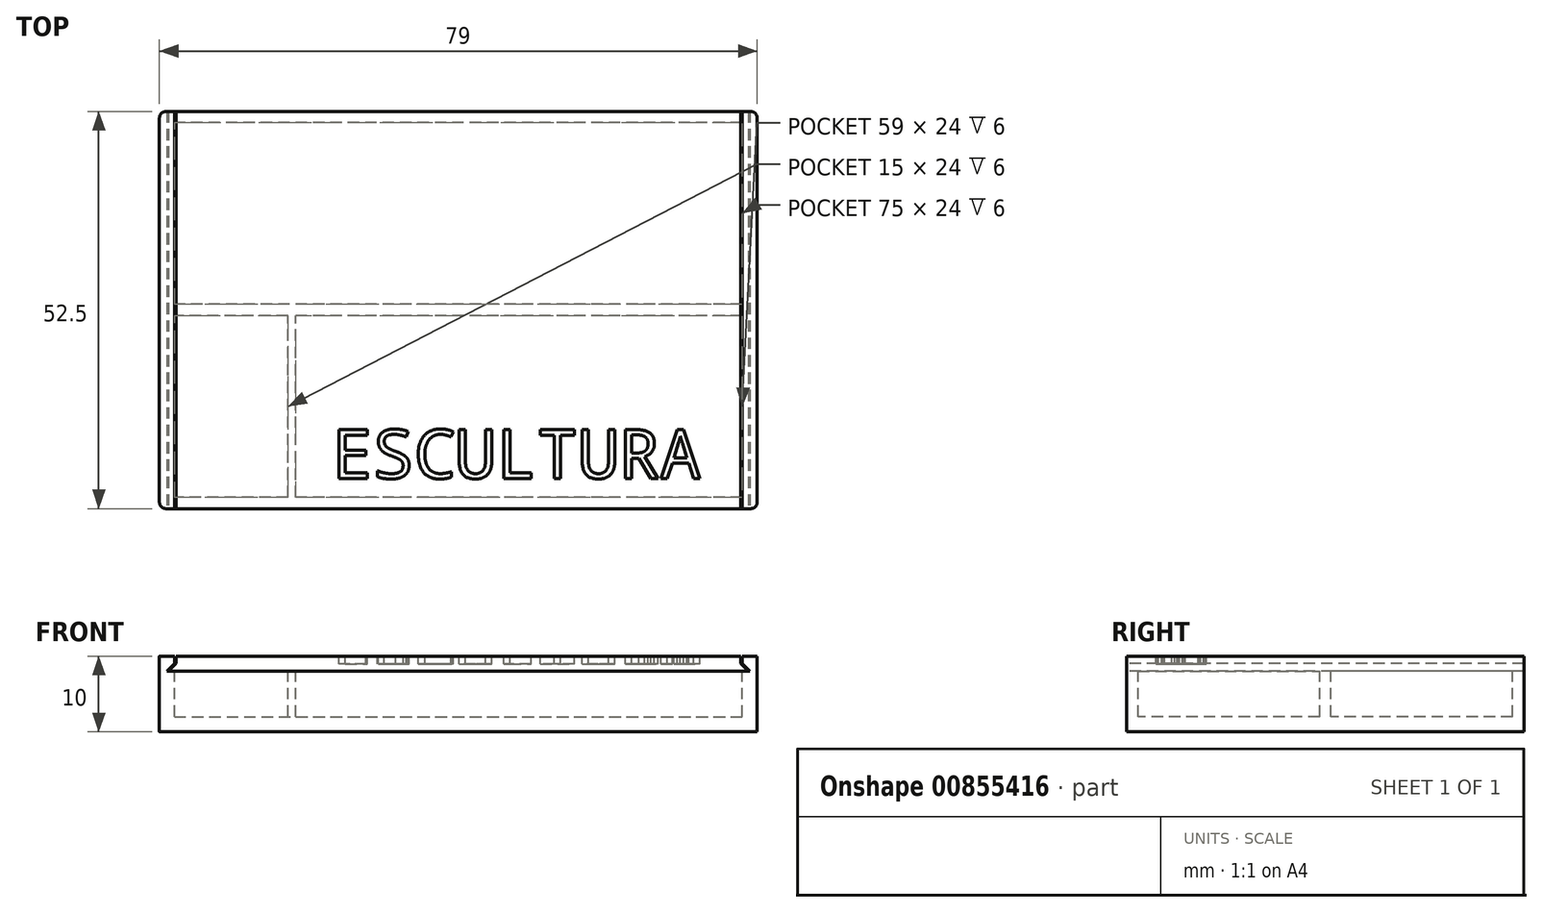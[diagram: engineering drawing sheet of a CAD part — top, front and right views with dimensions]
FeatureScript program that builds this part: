
annotation { "Feature Type Name" : "Feature", "Feature Type Description" : "" }
export const myFeature = defineFeature(function(context is Context, id is Id, definition is map)
    precondition{}
    {
        {
            var Q0;
            Q0=qCreatedBy(makeId("Top.planeOp"),FACE);
            var sketch = newSketch(context, id + "F0", { "sketchPlane" : qUnion([Q0])});
            skLineSegment(sketch, "E0.bottom", {"start": v(-39.5, 26.25) * mm, "end": v(39.5, 26.25) * mm});
            skLineSegment(sketch, "E0.top", {"start": v(-39.5, -26.25) * mm, "end": v(39.5, -26.25) * mm});
            skLineSegment(sketch, "E0.left", {"start": v(-39.5, 26.25) * mm, "end": v(-39.5, -26.25) * mm});
            skLineSegment(sketch, "E0.right", {"start": v(39.5, 26.25) * mm, "end": v(39.5, -26.25) * mm});
            skLineSegment(sketch, "E1", {"start": v(0, 0) * mm, "end": v(0, 26.25) * mm, "construction": true});
            skLineSegment(sketch, "E2", {"start": v(0, 0) * mm, "end": v(39.5, 0) * mm, "construction": true});
            skLineSegment(sketch, "E3.bottom", {"start": v(-37.5, 24.75) * mm, "end": v(37.5, 24.75) * mm});
            skLineSegment(sketch, "E3.top", {"start": v(-37.5, 0.75) * mm, "end": v(37.5, 0.75) * mm});
            skLineSegment(sketch, "E3.left", {"start": v(-37.5, 24.75) * mm, "end": v(-37.5, 0.75) * mm});
            skLineSegment(sketch, "E3.right", {"start": v(37.5, 24.75) * mm, "end": v(37.5, 0.75) * mm});
            skLineSegment(sketch, "E4.bottom", {"start": v(-37.5, -0.75) * mm, "end": v(-22.5, -0.75) * mm});
            skLineSegment(sketch, "E4.top", {"start": v(-37.5, -24.75) * mm, "end": v(-22.5, -24.75) * mm});
            skLineSegment(sketch, "E4.left", {"start": v(-37.5, -0.75) * mm, "end": v(-37.5, -24.75) * mm});
            skLineSegment(sketch, "E4.right", {"start": v(-22.5, -0.75) * mm, "end": v(-22.5, -24.75) * mm});
            skLineSegment(sketch, "E5.bottom", {"start": v(-21.5, -0.75) * mm, "end": v(37.5, -0.75) * mm});
            skLineSegment(sketch, "E5.top", {"start": v(-21.5, -24.75) * mm, "end": v(37.5, -24.75) * mm});
            skLineSegment(sketch, "E5.left", {"start": v(-21.5, -0.75) * mm, "end": v(-21.5, -24.75) * mm});
            skLineSegment(sketch, "E5.right", {"start": v(37.5, -0.75) * mm, "end": v(37.5, -24.75) * mm});
            skSolve(sketch);
        }
        {
            var Q0;
            Q0=makeQuery(id+"F0.imprint","IMPRINT",FACE,{"disambiguationData":[TD([[makeQuery(id+"F0.imprint","IMPRINT",EDGE,{"derivedFrom":sQuery(id+"F0.wireOp",EDGE,"E5.bottom")}),-1.0]])]});
            var Q1;
            Q1=makeQuery(id+"F0.imprint","IMPRINT",FACE,{"disambiguationData":[TD([[makeQuery(id+"F0.imprint","IMPRINT",EDGE,{"derivedFrom":sQuery(id+"F0.wireOp",EDGE,"E0.bottom")}),-1.0]])]});
            var Q2;
            Q2=makeQuery(id+"F0.imprint","IMPRINT",FACE,{"disambiguationData":[TD([[makeQuery(id+"F0.imprint","IMPRINT",EDGE,{"derivedFrom":sQuery(id+"F0.wireOp",EDGE,"E3.bottom")}),-1.0]])]});
            var Q3;
            Q3=makeQuery(id+"F0.imprint","IMPRINT",FACE,{"disambiguationData":[TD([[makeQuery(id+"F0.imprint","IMPRINT",EDGE,{"derivedFrom":sQuery(id+"F0.wireOp",EDGE,"E4.bottom")}),-1.0]])]});
            extrude(context, id + "F1", {"entities" : qUnion([Q0, Q1, Q2, Q3]), "oppositeDirection" : true, "depth" : 10 * mm, "offsetDistance" : 25 * mm});
        }
        {
            var Q0;
            Q0=makeQuery(id+"F0.imprint","IMPRINT",FACE,{"disambiguationData":[TD([[makeQuery(id+"F0.imprint","IMPRINT",EDGE,{"derivedFrom":sQuery(id+"F0.wireOp",EDGE,"E3.bottom")}),-1.0]])]});
            var Q1;
            Q1=makeQuery(id+"F0.imprint","IMPRINT",FACE,{"disambiguationData":[TD([[makeQuery(id+"F0.imprint","IMPRINT",EDGE,{"derivedFrom":sQuery(id+"F0.wireOp",EDGE,"E4.bottom")}),-1.0]])]});
            var Q2;
            Q2=makeQuery(id+"F0.imprint","IMPRINT",FACE,{"disambiguationData":[TD([[makeQuery(id+"F0.imprint","IMPRINT",EDGE,{"derivedFrom":sQuery(id+"F0.wireOp",EDGE,"E5.bottom")}),-1.0]])]});
            extrude(context, id + "F2", {"entities" : qUnion([Q0, Q1, Q2]), "operationType" : NewBodyOperationType.REMOVE, "oppositeDirection" : true, "depth" : 8 * mm, "offsetDistance" : 25 * mm});
        }
        {
            var Q0;
            Q0=makeQuery(id+"F0.imprint","IMPRINT",FACE,{"disambiguationData":[TD([[makeQuery(id+"F0.imprint","IMPRINT",EDGE,{"derivedFrom":sQuery(id+"F0.wireOp",EDGE,"E0.bottom")}),-1.0]])]});
            var sketch = newSketch(context, id + "F3", { "sketchPlane" : qUnion([Q0])});
            skLineSegment(sketch, "E6.0", {"start": v(-37.5, 25.25) * mm, "end": v(-37.5, 0.75) * mm});
            skLineSegment(sketch, "E6.1", {"start": v(37.5, 24.75) * mm, "end": v(37.5, 0.75) * mm});
            skLineSegment(sketch, "E7.0", {"start": v(-37.5, -0.75) * mm, "end": v(-37.5, -25.25) * mm});
            skLineSegment(sketch, "E7.1", {"start": v(37.5, -0.75) * mm, "end": v(37.5, -25.25) * mm});
            skLineSegment(sketch, "E8.bottom", {"start": v(-37.5, 27.25) * mm, "end": v(37.5, 27.25) * mm});
            skLineSegment(sketch, "E8.top", {"start": v(-37.5, -27.25) * mm, "end": v(37.5, -27.25) * mm});
            skLineSegment(sketch, "E8.left", {"start": v(-37.5, 27.25) * mm, "end": v(-37.5, -27.25) * mm});
            skLineSegment(sketch, "E8.right", {"start": v(37.5, 27.25) * mm, "end": v(37.5, -27.25) * mm});
            skSolve(sketch);
        }
        {
            var Q0;
            Q0 = qSketchRegion(id + "F3", true);
            extrude(context, id + "F4", {"entities" : qUnion([Q0]), "operationType" : NewBodyOperationType.REMOVE, "oppositeDirection" : true, "depth" : 2 * mm, "offsetDistance" : 25 * mm});
        }
        {
            var Q0;
            Q0=makeQuery(id+"F1.opExtrude","SWEPT_FACE",FACE,{"disambiguationData":[OSD([sQuery(id+"F0.wireOp",EDGE,"E0.top")])]});
            var sketch = newSketch(context, id + "F5", { "sketchPlane" : qUnion([Q0])});
            skLineSegment(sketch, "E9", {"start": v(-37.5, -2) * mm, "end": v(-38.5, -2) * mm});
            skLineSegment(sketch, "E10", {"start": v(-38.5, -2) * mm, "end": v(-37.5, -1) * mm});
            skLineSegment(sketch, "E11", {"start": v(-37.5, -1) * mm, "end": v(-37.5, -2) * mm});
            skLineSegment(sketch, "E12", {"start": v(0, 0) * mm, "end": v(0, -10) * mm, "construction": true});
            skLineSegment(sketch, "E13.MirrorCS", {"start": v(38.5, -2) * mm, "end": v(37.5, -1) * mm});
            skLineSegment(sketch, "E14.MirrorCS", {"start": v(37.5, -1) * mm, "end": v(37.5, -2) * mm});
            skLineSegment(sketch, "E15.MirrorCS", {"start": v(37.5, -2) * mm, "end": v(38.5, -2) * mm});
            skSolve(sketch);
        }
        {
            var Q0;
            Q0 = qSketchRegion(id + "F5", true);
            extrude(context, id + "F6", {"entities" : qUnion([Q0]), "operationType" : NewBodyOperationType.REMOVE, "endBound" : BoundingType.THROUGH_ALL, "oppositeDirection" : true, "depth" : 25 * mm, "offsetDistance" : 25 * mm});
        }
        {
            var Q0;
            Q0=makeQuery(id+"F1.opExtrude","SWEPT_FACE",FACE,{"disambiguationData":[OSD([sQuery(id+"F0.wireOp",EDGE,"E0.top")])]});
            var sketch = newSketch(context, id + "F7", { "sketchPlane" : qUnion([Q0])});
            skLineSegment(sketch, "E16", {"start": v(-37.3, 0) * mm, "end": v(-37.3, -1) * mm});
            skLineSegment(sketch, "E17", {"start": v(-37.3, -1) * mm, "end": v(-38.3, -2) * mm});
            skLineSegment(sketch, "E18", {"start": v(-38.3, -2) * mm, "end": v(38.3, -2) * mm});
            skLineSegment(sketch, "E19", {"start": v(38.3, -2) * mm, "end": v(37.3, -1) * mm});
            skLineSegment(sketch, "E20", {"start": v(37.3, -1) * mm, "end": v(37.3, 0) * mm});
            skLineSegment(sketch, "E21", {"start": v(37.3, 0) * mm, "end": v(-37.3, 0) * mm});
            skSolve(sketch);
        }
        {
            var Q0;
            Q0=makeQuery(id+"F7.imprint","IMPRINT",FACE,{"disambiguationData":[TD([[makeQuery(id+"F7.imprint","IMPRINT",EDGE,{"derivedFrom":sQuery(id+"F7.wireOp",EDGE,"E16")}),1.0]])]});
            var Q1;
            Q1=makeQuery(id+"F1.opExtrude","SWEPT_FACE",FACE,{"disambiguationData":[OSD([sQuery(id+"F0.wireOp",EDGE,"E0.bottom")])]});
            extrude(context, id + "F8", {"entities" : qUnion([Q0]), "endBound" : BoundingType.UP_TO_SURFACE, "oppositeDirection" : true, "depth" : 25 * mm, "endBoundEntityFace" : qUnion([Q1]), "offsetDistance" : 25 * mm});
        }
        {
            var Q0;
            Q0=makeQuery(id+"F1.opExtrude","SWEPT_EDGE",EDGE,{"disambiguationData":[OSD([sQuery(id+"F0.wireOp",EDGE,"E0.top"),sQuery(id+"F0.wireOp",EDGE,"E0.right")])]});
            var Q1;
            Q1=makeQuery(id+"F1.opExtrude","SWEPT_EDGE",EDGE,{"disambiguationData":[OSD([sQuery(id+"F0.wireOp",EDGE,"E0.top"),sQuery(id+"F0.wireOp",EDGE,"E0.left")])]});
            var Q2;
            Q2=makeQuery(id+"F1.opExtrude","SWEPT_EDGE",EDGE,{"disambiguationData":[OSD([sQuery(id+"F0.wireOp",EDGE,"E0.bottom"),sQuery(id+"F0.wireOp",EDGE,"E0.left")])]});
            var Q3;
            Q3=makeQuery(id+"F1.opExtrude","SWEPT_EDGE",EDGE,{"disambiguationData":[OSD([sQuery(id+"F0.wireOp",EDGE,"E0.bottom"),sQuery(id+"F0.wireOp",EDGE,"E0.right")])]});
            fillet(context, id + "F9", {"entities" : qUnion([Q0, Q1, Q2, Q3]), "radius" : 1 * mm, "tangentPropagation" : true, "rho" : 0.5, "crossSection" : FilletCrossSection.CONIC, "allowEdgeOverflow" : false});
        }
        {
            var Q0;
            Q0=makeQuery(id+"F8.opExtrude","SWEPT_FACE",FACE,{"disambiguationData":[OSD([sQuery(id+"F7.wireOp",EDGE,"E21")])]});
            var sketch = newSketch(context, id + "F10", { "sketchPlane" : qUnion([Q0])});
            skText(sketch, "E22", { "text": "ESCULTURA", "fontName": "DroidSansMono.ttf"});
            skLineSegment(sketch, "E23", {"start": v(33.3, -22.25) * mm, "end": v(37.3, -22.25) * mm, "construction": true});
            skLineSegment(sketch, "E24", {"start": v(33.3, -22.25) * mm, "end": v(33.3, -26.25) * mm, "construction": true});
            const initialGuessF10  = {"E22": [-0.0167, -0.02225, 1, 0, 0.0065]};
            skSetInitialGuess(sketch, initialGuessF10);
            skSolve(sketch);
        }
        {
            var Q0;
            Q0 = qSketchRegion(id + "F10", true);
            extrude(context, id + "F11", {"entities" : qUnion([Q0]), "operationType" : NewBodyOperationType.REMOVE, "oppositeDirection" : true, "depth" : 1 * mm, "offsetDistance" : 25 * mm});
        }
    });
